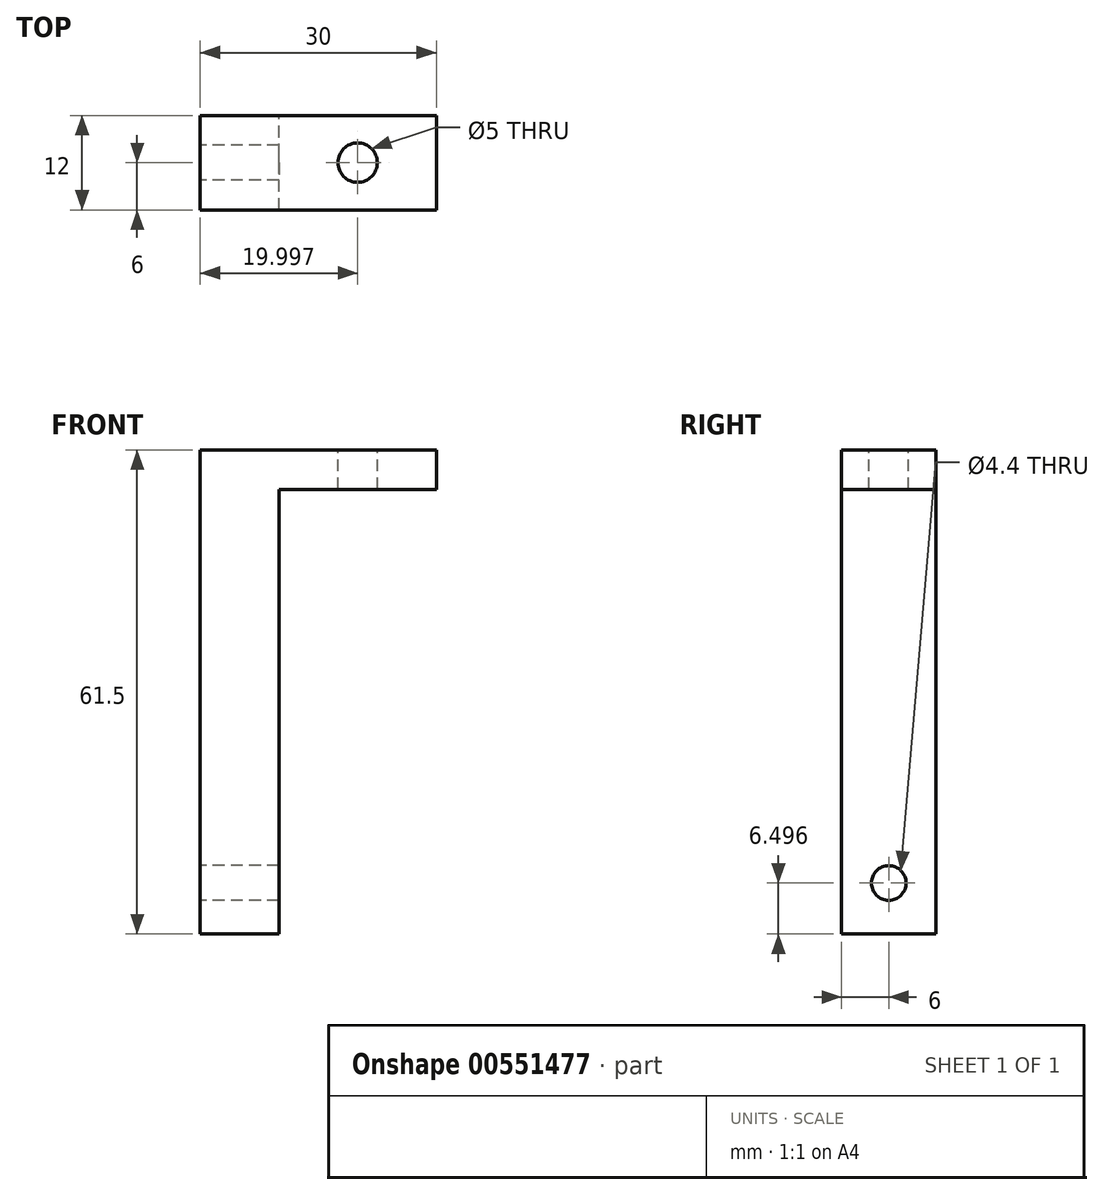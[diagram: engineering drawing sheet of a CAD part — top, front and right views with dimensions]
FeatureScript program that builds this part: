
annotation { "Feature Type Name" : "Feature", "Feature Type Description" : "" }
export const myFeature = defineFeature(function(context is Context, id is Id, definition is map)
    precondition{}
    {
        {
            var Q0;
            Q0=qCreatedBy(makeId("Front.planeOp"),FACE);
            var sketch = newSketch(context, id + "F0", { "sketchPlane" : qUnion([Q0])});
            skLineSegment(sketch, "E0", {"start": v(-31.52, 71.1) * mm, "end": v(-1.52, 71.1) * mm});
            skLineSegment(sketch, "E1", {"start": v(-1.52, 71.1) * mm, "end": v(-1.52, 66.1) * mm});
            skLineSegment(sketch, "E2", {"start": v(-1.52, 66.1) * mm, "end": v(-21.52, 66.1) * mm});
            skLineSegment(sketch, "E3", {"start": v(-21.52, 66.1) * mm, "end": v(-21.52, 9.6) * mm});
            skLineSegment(sketch, "E4", {"start": v(-21.52, 9.6) * mm, "end": v(-31.52, 9.6) * mm});
            skLineSegment(sketch, "E5", {"start": v(-31.52, 9.6) * mm, "end": v(-31.52, 71.1) * mm});
            skSolve(sketch);
        }
        {
            var Q0;
            Q0=makeQuery(id+"F0.imprint","IMPRINT",FACE,{"disambiguationData":[TD([[makeQuery(id+"F0.imprint","IMPRINT",EDGE,{"derivedFrom":sQuery(id+"F0.wireOp",EDGE,"E0")}),-1.0]])]});
            extrude(context, id + "F1", {"entities" : qUnion([Q0]), "depth" : 12 * mm, "offsetDistance" : 25 * mm});
        }
        {
            var Q0;
            Q0=makeQuery(id+"F1.opExtrude","SWEPT_FACE",FACE,{"disambiguationData":[OSD([sQuery(id+"F0.wireOp",EDGE,"E5")])]});
            var sketch = newSketch(context, id + "F2", { "sketchPlane" : qUnion([Q0])});
            skLineSegment(sketch, "E6.0", {"start": v(12, 66.1) * mm, "end": v(0, 66.1) * mm});
            skLineSegment(sketch, "E7.0", {"start": v(12, 16.1) * mm, "end": v(0, 16.1) * mm});
            skCircle(sketch, "E8", {"center": v(6, 16.1) * mm, "radius": 2.2 * mm});
            skSolve(sketch);
        }
        {
            var Q0;
            {var subQ0=sQuery(id+"F2.wireOp",EDGE,"E8");var subQ1=sQuery(id+"F2.wireOp",EDGE,"E7.0");var subQ2=makeQuery(id+"F2.imprint","INTERSECT",VERTEX,{"disambiguationData":[OD(0.0)],"derivedFrom":[subQ1,subQ0]});Q0=makeQuery(id+"F2.imprint","IMPRINT",FACE,{"disambiguationData":[TD([[makeQuery(id+"F2.imprint","IMPRINT",EDGE,{"disambiguationData":[TD([[subQ2,-1.0]])],"derivedFrom":subQ1}),1.0]])]});}
            var Q1;
            {var subQ0=sQuery(id+"F2.wireOp",EDGE,"E8");var subQ1=sQuery(id+"F2.wireOp",EDGE,"E7.0");var subQ2=makeQuery(id+"F2.imprint","INTERSECT",VERTEX,{"disambiguationData":[OD(0.0)],"derivedFrom":[subQ1,subQ0]});Q1=makeQuery(id+"F2.imprint","IMPRINT",FACE,{"disambiguationData":[TD([[makeQuery(id+"F2.imprint","IMPRINT",EDGE,{"disambiguationData":[TD([[subQ2,-1.0]])],"derivedFrom":subQ1}),-1.0]])]});}
            extrude(context, id + "F3", {"entities" : qUnion([Q0, Q1]), "operationType" : NewBodyOperationType.REMOVE, "oppositeDirection" : true, "depth" : 25 * mm, "offsetDistance" : 25 * mm});
        }
        {
            var Q0;
            Q0=makeQuery(id+"F1.opExtrude","SWEPT_FACE",FACE,{"disambiguationData":[OSD([sQuery(id+"F0.wireOp",EDGE,"E0")])]});
            var sketch = newSketch(context, id + "F4", { "sketchPlane" : qUnion([Q0])});
            skLineSegment(sketch, "E9.0", {"start": v(-21.52, -12) * mm, "end": v(-21.52, 0) * mm});
            skLineSegment(sketch, "E10", {"start": v(-21.52, -12) * mm, "end": v(-1.52, 0) * mm});
            skCircle(sketch, "E11", {"center": v(-11.52, -6) * mm, "radius": 2.5 * mm});
            skSolve(sketch);
        }
        {
            var Q0;
            {var subQ0=sQuery(id+"F4.wireOp",EDGE,"E11");var subQ1=sQuery(id+"F4.wireOp",EDGE,"E10");var subQ2=makeQuery(id+"F4.imprint","INTERSECT",VERTEX,{"disambiguationData":[OD(0.0)],"derivedFrom":[subQ1,subQ0]});Q0=makeQuery(id+"F4.imprint","IMPRINT",FACE,{"disambiguationData":[TD([[makeQuery(id+"F4.imprint","IMPRINT",EDGE,{"disambiguationData":[TD([[subQ2,-1.0]])],"derivedFrom":subQ1}),1.0]])]});}
            var Q1;
            {var subQ0=sQuery(id+"F4.wireOp",EDGE,"E11");var subQ1=sQuery(id+"F4.wireOp",EDGE,"E10");var subQ2=makeQuery(id+"F4.imprint","INTERSECT",VERTEX,{"disambiguationData":[OD(0.0)],"derivedFrom":[subQ1,subQ0]});Q1=makeQuery(id+"F4.imprint","IMPRINT",FACE,{"disambiguationData":[TD([[makeQuery(id+"F4.imprint","IMPRINT",EDGE,{"disambiguationData":[TD([[subQ2,-1.0]])],"derivedFrom":subQ1}),-1.0]])]});}
            extrude(context, id + "F5", {"entities" : qUnion([Q0, Q1]), "operationType" : NewBodyOperationType.REMOVE, "oppositeDirection" : true, "depth" : 25 * mm, "offsetDistance" : 25 * mm});
        }
    });
